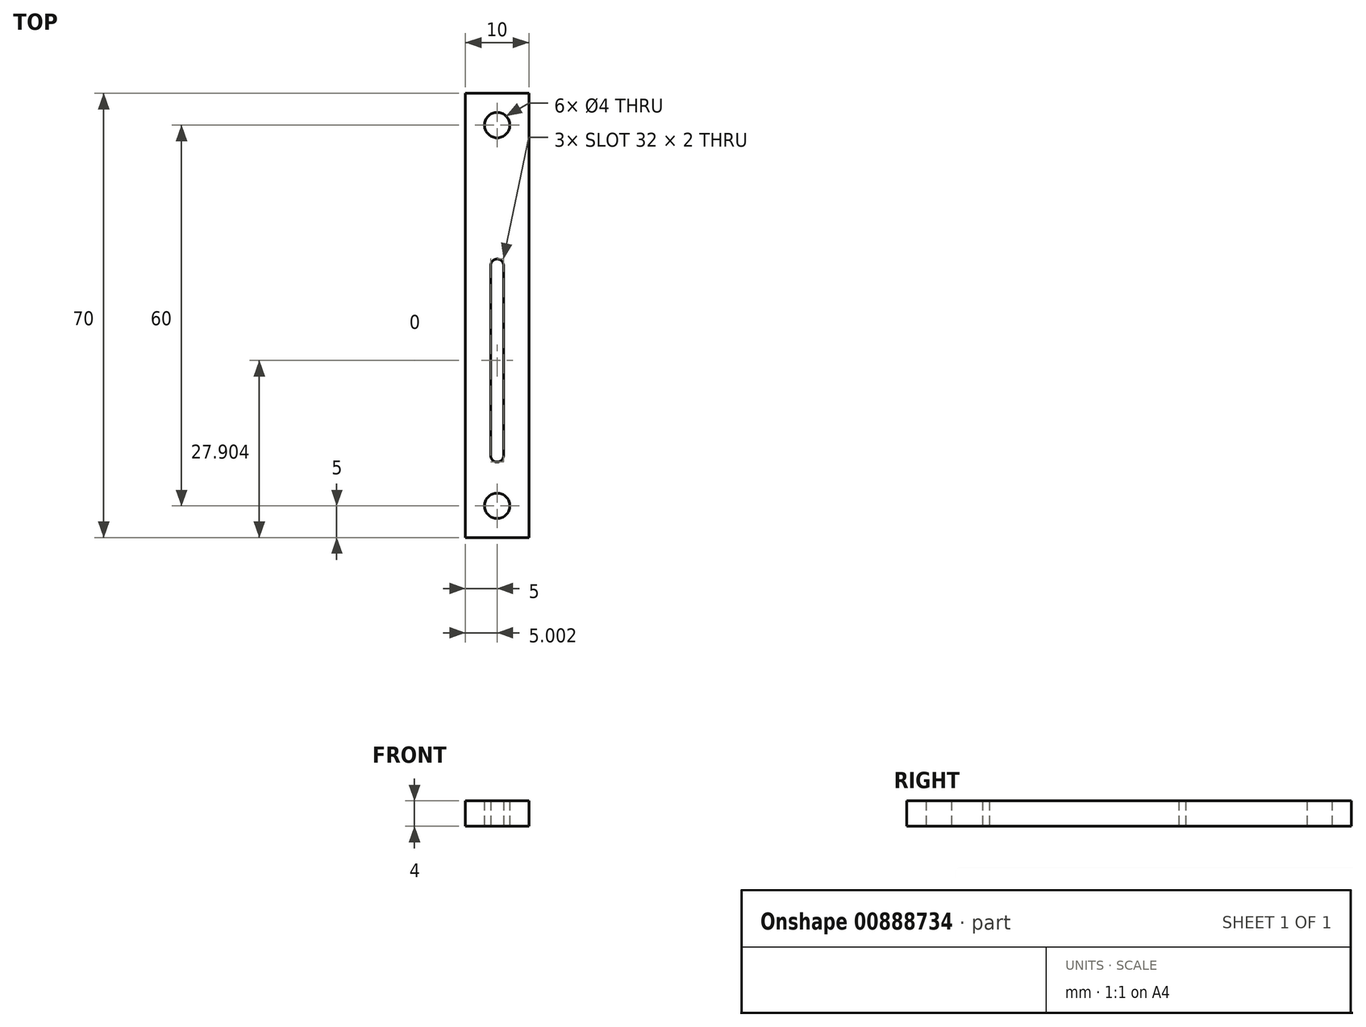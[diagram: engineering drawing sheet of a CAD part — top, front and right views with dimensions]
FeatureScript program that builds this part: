
annotation { "Feature Type Name" : "Feature", "Feature Type Description" : "" }
export const myFeature = defineFeature(function(context is Context, id is Id, definition is map)
    precondition{}
    {
        {
            var Q0;
            Q0=qCreatedBy(makeId("Top.planeOp"),FACE);
            var sketch = newSketch(context, id + "F0", { "sketchPlane" : qUnion([Q0])});
            skCircle(sketch, "E0", {"center": v(0, 0) * mm, "radius": 2 * mm});
            skLineSegment(sketch, "E1.bottom", {"start": v(-5, -5) * mm, "end": v(5, -5) * mm});
            skLineSegment(sketch, "E1.top", {"start": v(-5, 65) * mm, "end": v(5, 65) * mm});
            skLineSegment(sketch, "E1.left", {"start": v(-5, -5) * mm, "end": v(-5, 65) * mm});
            skLineSegment(sketch, "E1.right", {"start": v(5, -5) * mm, "end": v(5, 65) * mm});
            skCircle(sketch, "E2", {"center": v(0, 60) * mm, "radius": 2 * mm});
            skPoint(sketch, "E3", {"position": v(0, -5) * mm});
            skCircle(sketch, "E4", {"center": v(0, 7.9) * mm, "radius": 1 * mm});
            skCircle(sketch, "E5", {"center": v(0, 37.9) * mm, "radius": 1 * mm});
            skLineSegment(sketch, "E6", {"start": v(1, 7.9) * mm, "end": v(1, 37.9) * mm});
            skLineSegment(sketch, "E7", {"start": v(-1, 37.82) * mm, "end": v(-1, 7.99) * mm});
            skSolve(sketch);
        }
        {
            var Q0;
            Q0 = qSketchRegion(id + "F0", true);
            extrude(context, id + "F1", {"entities" : qUnion([Q0]), "endBound" : BoundingType.SYMMETRIC, "depth" : 4 * mm, "offsetDistance" : 25 * mm});
        }
    });
